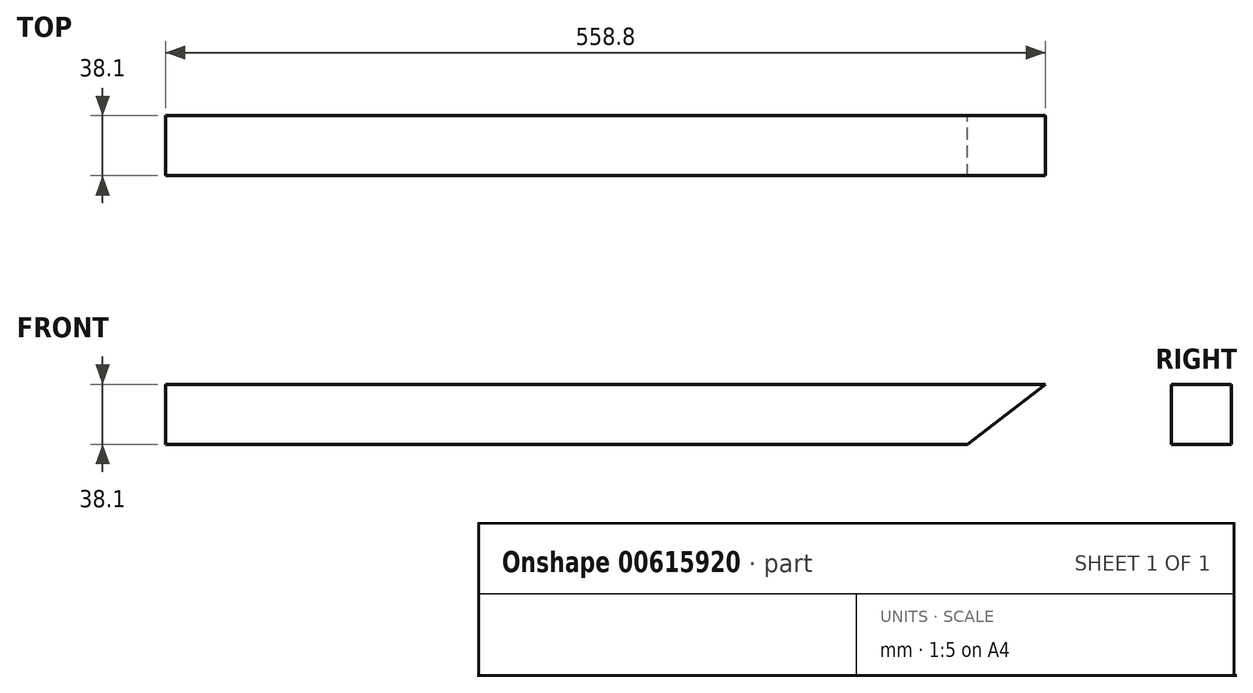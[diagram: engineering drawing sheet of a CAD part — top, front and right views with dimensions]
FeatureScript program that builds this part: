
annotation { "Feature Type Name" : "Feature", "Feature Type Description" : "" }
export const myFeature = defineFeature(function(context is Context, id is Id, definition is map)
    precondition{}
    {
        {
            var Q0;
            Q0=qCreatedBy(makeId("Front.planeOp"),FACE);
            var sketch = newSketch(context, id + "F0", { "sketchPlane" : qUnion([Q0])});
            skLineSegment(sketch, "E0.bottom", {"start": v(-279.4, 19.05) * mm, "end": v(279.4, 19.05) * mm});
            skLineSegment(sketch, "E0.left", {"start": v(-279.4, 19.05) * mm, "end": v(-279.4, -19.05) * mm});
            skPoint(sketch, "E0.middle", {"position": v(0, 0) * mm});
            skLineSegment(sketch, "E1", {"start": v(279.4, 19.05) * mm, "end": v(229.75, -19.05) * mm});
            skLineSegment(sketch, "E2", {"start": v(229.75, -19.05) * mm, "end": v(-279.4, -19.05) * mm});
            skSolve(sketch);
        }
        {
            var Q0;
            Q0 = qSketchRegion(id + "F0", true);
            extrude(context, id + "F1", {"entities" : qUnion([Q0]), "endBound" : BoundingType.SYMMETRIC, "depth" : 38.1 * mm, "offsetDistance" : 25.4 * mm});
        }
    });
